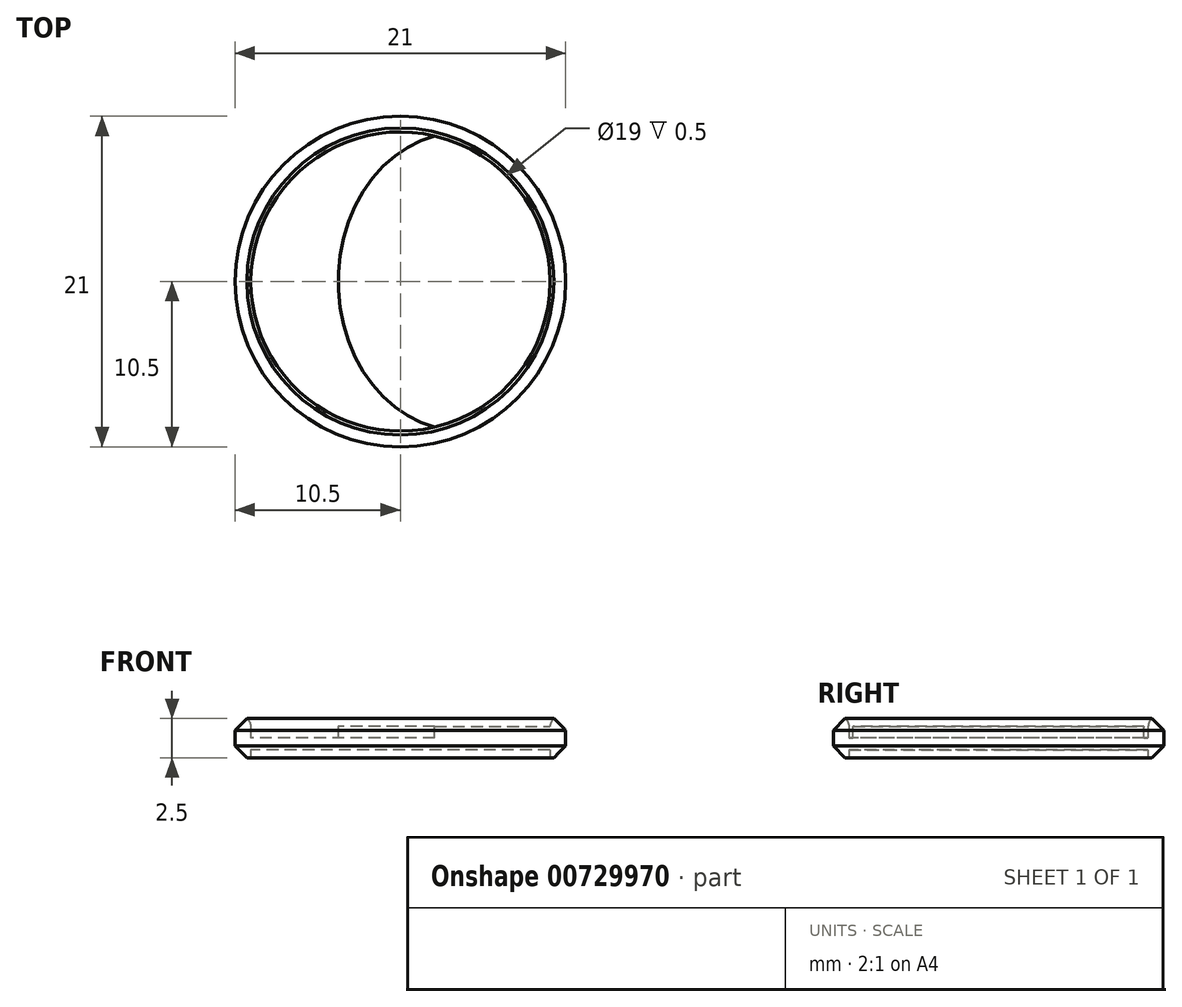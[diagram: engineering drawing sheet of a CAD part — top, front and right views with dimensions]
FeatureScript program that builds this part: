
annotation { "Feature Type Name" : "Feature", "Feature Type Description" : "" }
export const myFeature = defineFeature(function(context is Context, id is Id, definition is map)
    precondition{}
    {
        {
            var Q0;
            Q0=qCreatedBy(makeId("Top.planeOp"),FACE);
            var sketch = newSketch(context, id + "F0", { "sketchPlane" : qUnion([Q0])});
            skCircle(sketch, "E0", {"center": v(0, 0) * mm, "radius": 10 * mm});
            skSolve(sketch);
        }
        {
            var Q0;
            Q0=makeQuery(id+"F0.imprint","IMPRINT",FACE,{"disambiguationData":[TD([[makeQuery(id+"F0.imprint","IMPRINT",EDGE,{"derivedFrom":sQuery(id+"F0.wireOp",EDGE,"E0")}),1.0]])]});
            extrude(context, id + "F1", {"entities" : qUnion([Q0]), "depth" : 1.5 * mm, "offsetDistance" : 25 * mm});
        }
        {
            var Q0;
            Q0=makeQuery(id+"F1.opExtrude","CAP_FACE",FACE,{"disambiguationData":[OSD([sQuery(id+"F0.wireOp",EDGE,"E0")])],"isStart":false});
            var sketch = newSketch(context, id + "F2", { "sketchPlane" : qUnion([Q0])});
            skEllipse(sketch, "E1", {"center": v(3.87, 0) * mm, "majorRadius": 7.82 * mm, "minorRadius": 9.47 * mm, "majorAxis": v(1, 0)});
            skSolve(sketch);
        }
        {
            var Q0;
            {var subQ0=sQuery(id+"F2.wireOp",EDGE,"E1");var subQ1=makeQuery(id+"F1.opExtrude","CAP_EDGE",EDGE,{"disambiguationData":[OSD([sQuery(id+"F0.wireOp",EDGE,"E0")])],"isStart":false});var subQ2=makeQuery(id+"F2.imprint","INTERSECT",VERTEX,{"disambiguationData":[OD(0.0)],"derivedFrom":[subQ1,subQ0]});Q0=makeQuery(id+"F2.imprint","IMPRINT",FACE,{"disambiguationData":[TD([[makeQuery(id+"F2.imprint","IMPRINT",EDGE,{"disambiguationData":[TD([[subQ2,1.0]])],"derivedFrom":subQ0}),-1.0]])]});}
            extrude(context, id + "F3", {"entities" : qUnion([Q0]), "operationType" : NewBodyOperationType.REMOVE, "oppositeDirection" : true, "depth" : 0.75 * mm, "offsetDistance" : 25 * mm});
        }
        {
            var Q0;
            Q0=qCreatedBy(makeId("Top.planeOp"),FACE);
            var sketch = newSketch(context, id + "F4", { "sketchPlane" : qUnion([Q0])});
            skCircle(sketch, "E2", {"center": v(0, 0) * mm, "radius": 10.5 * mm});
            skCircle(sketch, "E3.0", {"center": v(0, 0) * mm, "radius": 9.5 * mm});
            skSolve(sketch);
        }
        {
            var Q0;
            Q0 = qSketchRegion(id + "F4", true);
            extrude(context, id + "F5", {"entities" : qUnion([Q0]), "operationType" : NewBodyOperationType.ADD, "depth" : 2 * mm, "offsetDistance" : 25 * mm, "hasSecondDirection" : true, "secondDirectionOppositeDirection" : true, "secondDirectionDepth" : 0.5 * mm});
        }
        {
            var Q0;
            Q0=makeQuery(id+"F5.opExtrude","CAP_EDGE",EDGE,{"disambiguationData":[OSD([sQuery(id+"F4.wireOp",EDGE,"E2")])],"isStart":false});
            var Q1;
            Q1=makeQuery(id+"F5.opExtrude","CAP_EDGE",EDGE,{"disambiguationData":[OSD([sQuery(id+"F4.wireOp",EDGE,"E2")])],"isStart":true});
            chamfer(context, id + "F6", {"entities" : qUnion([Q0, Q1]), "width" : 0.75 * mm, "tangentPropagation" : true});
        }
        {
            var Q0;
            Q0=makeQuery(id+"F5.opExtrude","CAP_EDGE",EDGE,{"disambiguationData":[OSD([sQuery(id+"F4.wireOp",EDGE,"E3.0")])],"isStart":false});
            fillet(context, id + "F7", {"entities" : qUnion([Q0]), "radius" : 0.75 * mm, "tangentPropagation" : true, "allowEdgeOverflow" : false});
        }
    });
